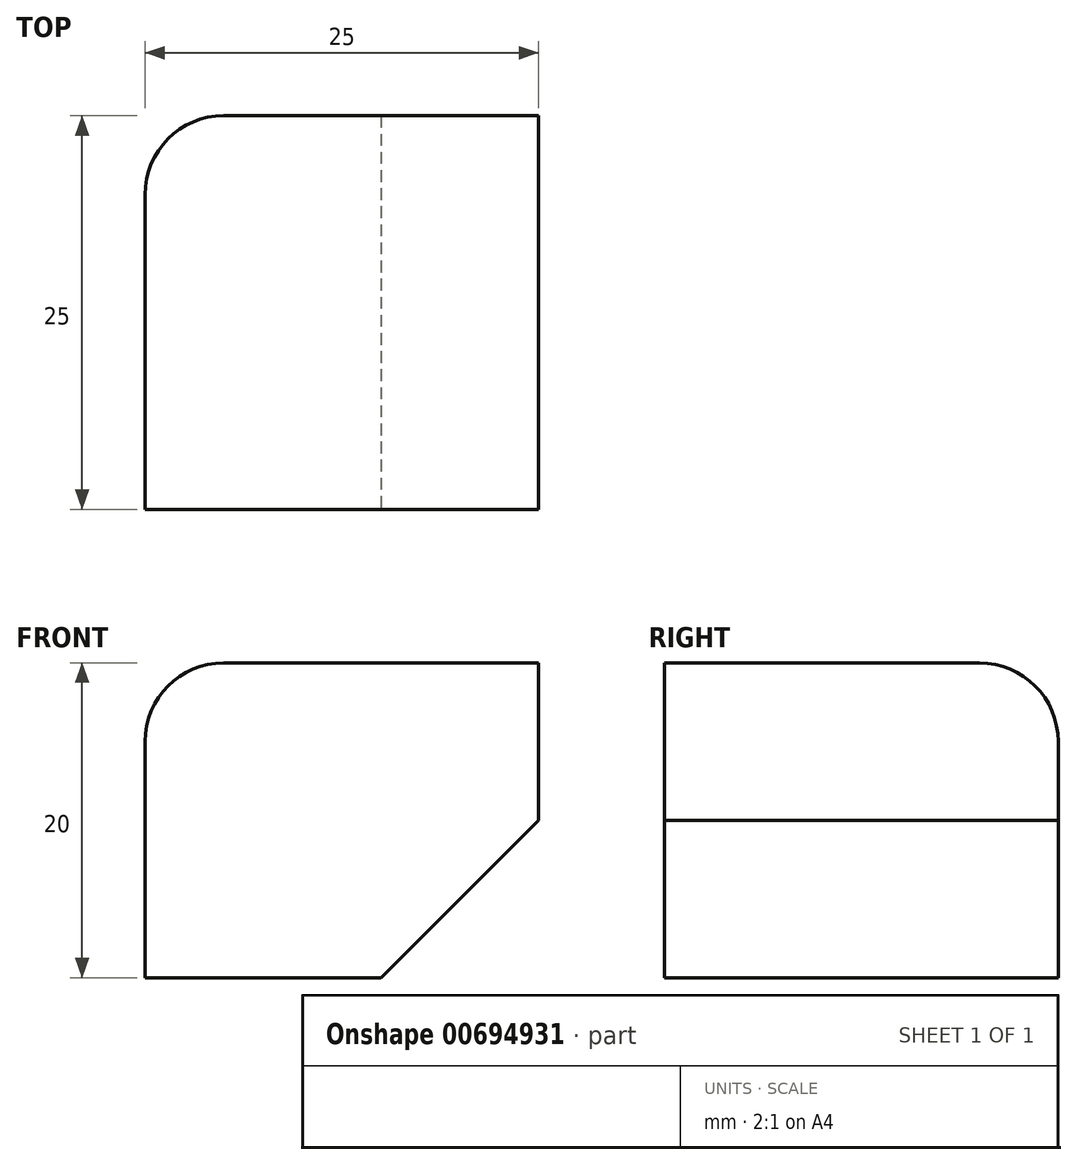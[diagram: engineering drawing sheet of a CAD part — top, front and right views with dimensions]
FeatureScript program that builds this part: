
annotation { "Feature Type Name" : "Feature", "Feature Type Description" : "" }
export const myFeature = defineFeature(function(context is Context, id is Id, definition is map)
    precondition{}
    {
        {
            var Q0;
            Q0=qCreatedBy(makeId("Top.planeOp"),FACE);
            var sketch = newSketch(context, id + "F0", { "sketchPlane" : qUnion([Q0])});
            skLineSegment(sketch, "E0.bottom", {"start": v(12.5, 12.5) * mm, "end": v(-12.5, 12.5) * mm});
            skLineSegment(sketch, "E0.top", {"start": v(12.5, -12.5) * mm, "end": v(-12.5, -12.5) * mm});
            skLineSegment(sketch, "E0.left", {"start": v(12.5, 12.5) * mm, "end": v(12.5, -12.5) * mm});
            skLineSegment(sketch, "E0.right", {"start": v(-12.5, 12.5) * mm, "end": v(-12.5, -12.5) * mm});
            skPoint(sketch, "E0.middle", {"position": v(0, 0) * mm});
            skSolve(sketch);
        }
        {
            var Q0;
            Q0=makeQuery(id+"F0.imprint","IMPRINT",FACE,{"disambiguationData":[TD([[makeQuery(id+"F0.imprint","IMPRINT",EDGE,{"derivedFrom":sQuery(id+"F0.wireOp",EDGE,"E0.bottom")}),1.0]])]});
            extrude(context, id + "F1", {"entities" : qUnion([Q0]), "depth" : 20 * mm, "offsetDistance" : 25 * mm});
        }
        {
            var Q0;
            Q0=makeQuery(id+"F1.opExtrude","SWEPT_EDGE",EDGE,{"disambiguationData":[OSD([sQuery(id+"F0.wireOp",EDGE,"E0.bottom"),sQuery(id+"F0.wireOp",EDGE,"E0.right")])]});
            var Q1;
            Q1=makeQuery(id+"F1.opExtrude","CAP_EDGE",EDGE,{"disambiguationData":[OSD([sQuery(id+"F0.wireOp",EDGE,"E0.right")])],"isStart":false});
            var Q2;
            Q2=makeQuery(id+"F1.opExtrude","CAP_EDGE",EDGE,{"disambiguationData":[OSD([sQuery(id+"F0.wireOp",EDGE,"E0.bottom")])],"isStart":false});
            fillet(context, id + "F2", {"entities" : qUnion([Q0, Q1, Q2]), "radius" : 5 * mm, "tangentPropagation" : true, "allowEdgeOverflow" : false});
        }
        {
            var Q0;
            Q0=makeQuery(id+"F1.opExtrude","CAP_EDGE",EDGE,{"disambiguationData":[OSD([sQuery(id+"F0.wireOp",EDGE,"E0.left")])],"isStart":true});
            chamfer(context, id + "F3", {"entities" : qUnion([Q0]), "width" : 10 * mm, "tangentPropagation" : true});
        }
    });
